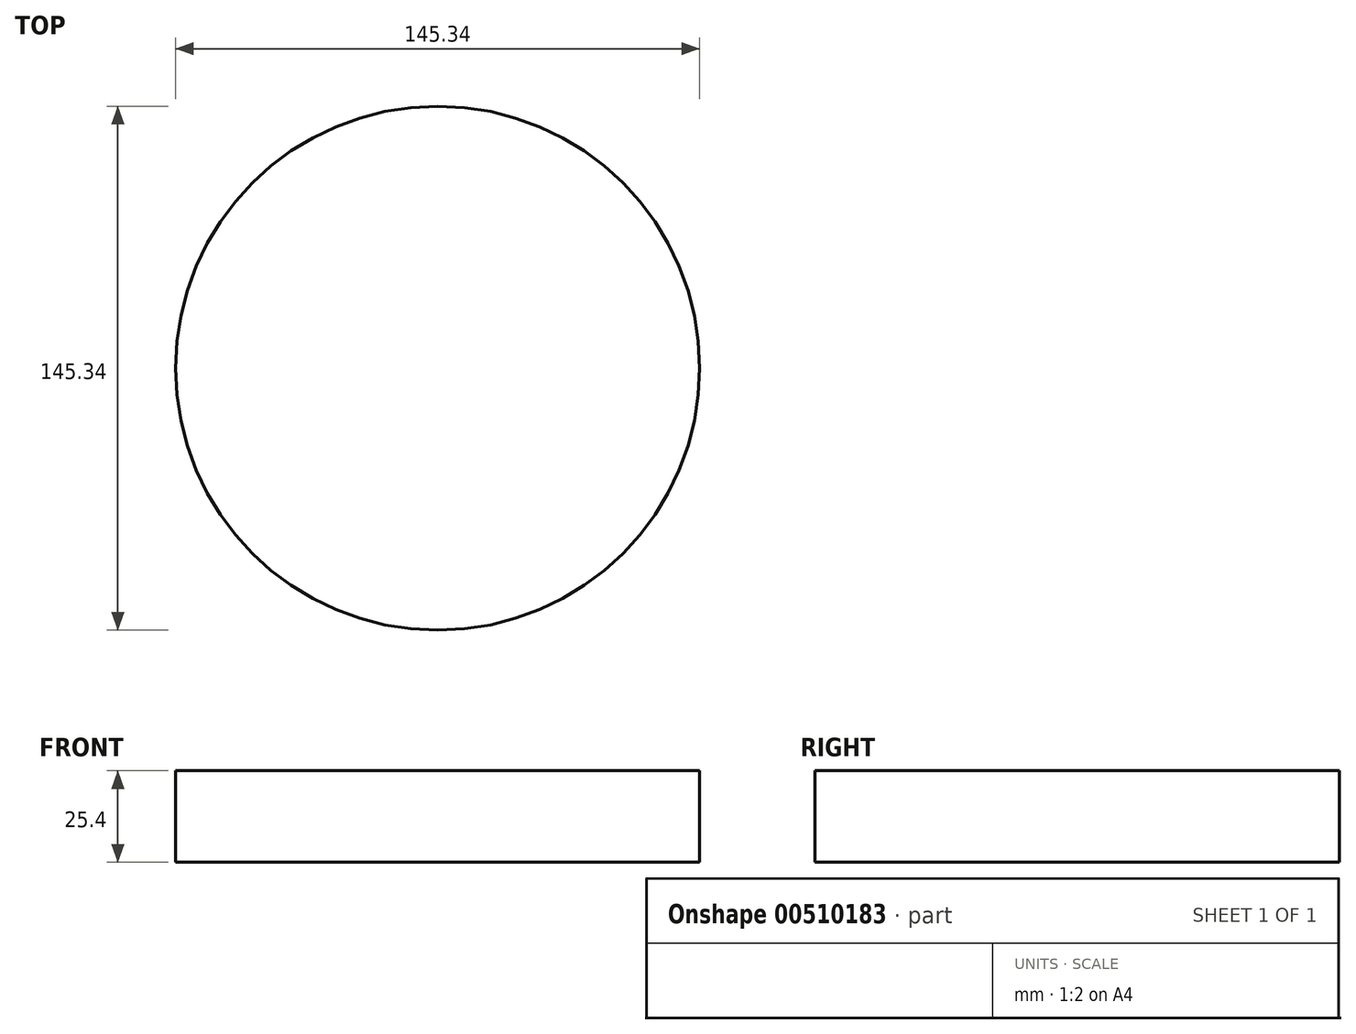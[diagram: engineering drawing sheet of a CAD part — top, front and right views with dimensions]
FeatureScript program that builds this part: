
annotation { "Feature Type Name" : "Feature", "Feature Type Description" : "" }
export const myFeature = defineFeature(function(context is Context, id is Id, definition is map)
    precondition{}
    {
        {
            var Q0;
            Q0=qCreatedBy(makeId("Top.planeOp"),FACE);
            var sketch = newSketch(context, id + "F0", { "sketchPlane" : qUnion([Q0])});
            skCircle(sketch, "E0", {"center": v(0, 0) * mm, "radius": 72.67 * mm});
            skSolve(sketch);
        }
        {
            var Q0;
            Q0=makeQuery(id+"F0.imprint","IMPRINT",FACE,{"disambiguationData":[TD([[makeQuery(id+"F0.imprint","IMPRINT",EDGE,{"derivedFrom":sQuery(id+"F0.wireOp",EDGE,"E0")}),1.0]])]});
            extrude(context, id + "F1", {"entities" : qUnion([Q0]), "depth" : 25.4 * mm});
        }
    });
